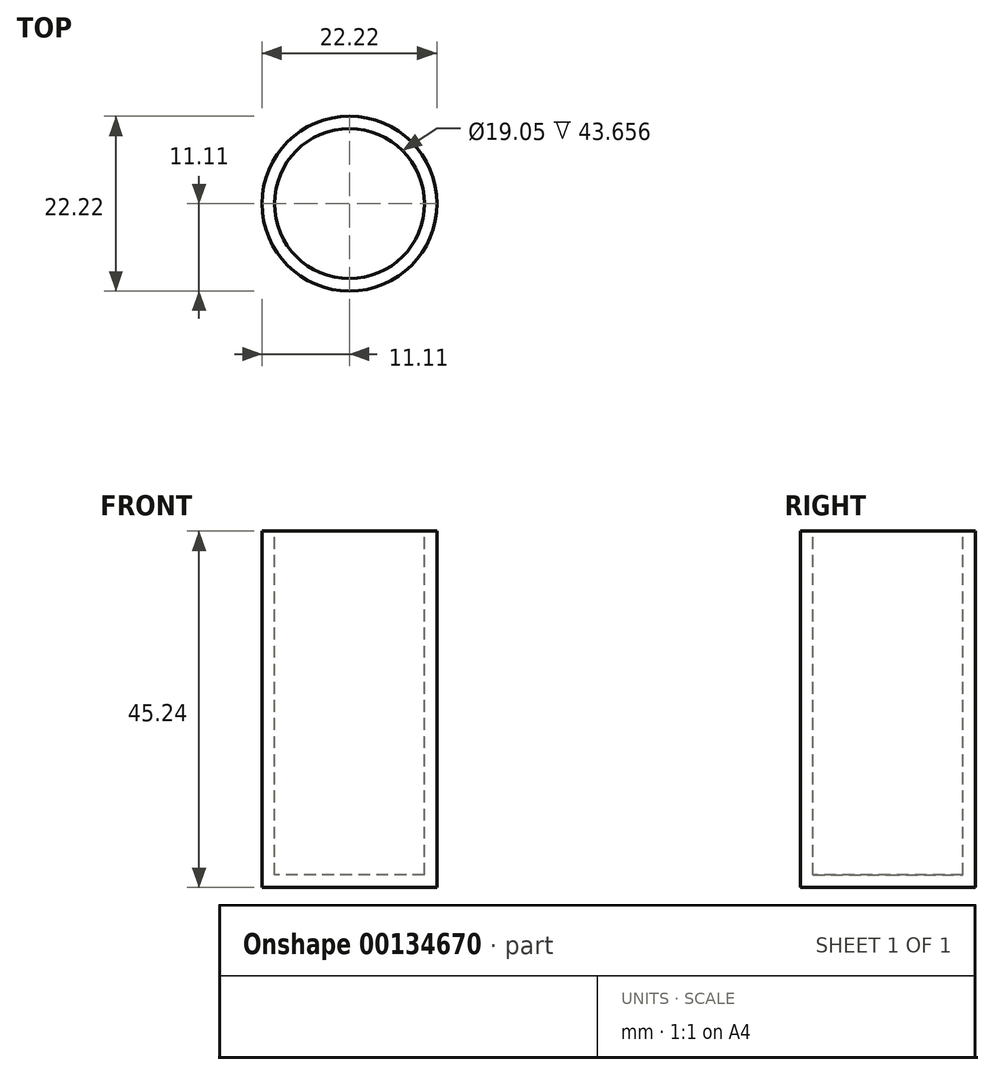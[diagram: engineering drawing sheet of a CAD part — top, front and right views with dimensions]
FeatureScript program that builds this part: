
annotation { "Feature Type Name" : "Feature", "Feature Type Description" : "" }
export const myFeature = defineFeature(function(context is Context, id is Id, definition is map)
    precondition{}
    {
        {
            var Q0;
            Q0=qCreatedBy(makeId("Front.planeOp"),FACE);
            var sketch = newSketch(context, id + "F0", { "sketchPlane" : qUnion([Q0])});
            skLineSegment(sketch, "E0", {"start": v(-6.64, 0) * mm, "end": v(-17.75, 0) * mm});
            skLineSegment(sketch, "E1", {"start": v(-17.75, 0) * mm, "end": v(-17.75, 45.24) * mm});
            skLineSegment(sketch, "E2", {"start": v(-17.75, 45.24) * mm, "end": v(-16.17, 45.24) * mm});
            skLineSegment(sketch, "E3", {"start": v(-16.17, 45.24) * mm, "end": v(-16.17, 1.59) * mm});
            skLineSegment(sketch, "E4", {"start": v(-16.17, 1.59) * mm, "end": v(-6.64, 1.59) * mm});
            skLineSegment(sketch, "E5", {"start": v(-6.64, 1.59) * mm, "end": v(-6.64, 0) * mm});
            skSolve(sketch);
        }
        {
            var Q0;
            Q0=qSketchRegion(id+"F0",true);
            var Q1;
            Q1=sQuery(id+"F0.wireOp",EDGE,"E5");
            revolve(context, id + "F1", {"entities" : qUnion([Q0]), "axis" : qUnion([Q1]), "revolveType" : RevolveType.FULL});
        }
    });
